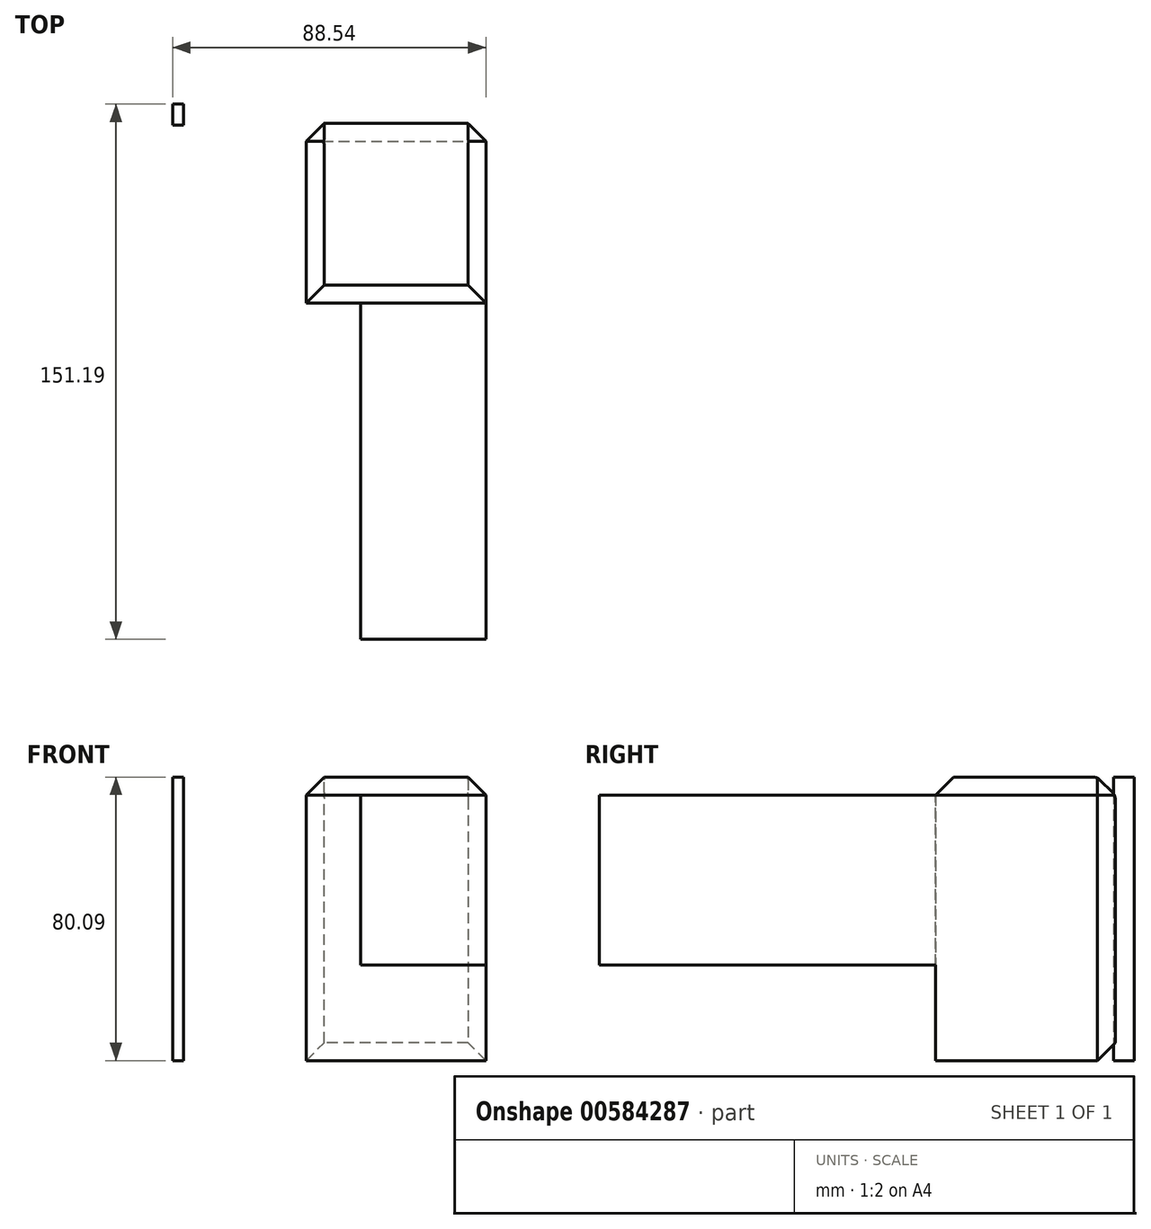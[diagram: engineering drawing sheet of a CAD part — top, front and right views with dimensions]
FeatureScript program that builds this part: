
annotation { "Feature Type Name" : "Feature", "Feature Type Description" : "" }
export const myFeature = defineFeature(function(context is Context, id is Id, definition is map)
    precondition{}
    {
        {
            var Q0;
            Q0=qCreatedBy(makeId("Top.planeOp"),FACE);
            var sketch = newSketch(context, id + "F0", { "sketchPlane" : qUnion([Q0])});
            skLineSegment(sketch, "E0.bottom", {"start": v(-37.74, 29.84) * mm, "end": v(-34.65, 29.84) * mm});
            skLineSegment(sketch, "E0.top", {"start": v(-37.74, 23.95) * mm, "end": v(-34.65, 23.95) * mm});
            skLineSegment(sketch, "E0.left", {"start": v(-37.74, 29.84) * mm, "end": v(-37.74, 23.95) * mm});
            skLineSegment(sketch, "E0.right", {"start": v(-34.65, 29.84) * mm, "end": v(-34.65, 23.95) * mm});
            skLineSegment(sketch, "E1.bottom", {"start": v(0, 24.42) * mm, "end": v(50.8, 24.42) * mm});
            skLineSegment(sketch, "E1.top", {"start": v(0, -26.38) * mm, "end": v(50.8, -26.38) * mm});
            skLineSegment(sketch, "E1.left", {"start": v(0, 24.42) * mm, "end": v(0, -26.38) * mm});
            skLineSegment(sketch, "E1.right", {"start": v(50.8, 24.42) * mm, "end": v(50.8, -26.38) * mm});
            skSolve(sketch);
        }
        {
            var Q0;
            Q0 = qSketchRegion(id + "F0", true);
            extrude(context, id + "F1", {"entities" : qUnion([Q0]), "depth" : 80.1 * mm, "offsetDistance" : 25.4 * mm});
        }
        {
            var Q0;
            Q0=makeQuery(id+"F1.opExtrude","CAP_EDGE",EDGE,{"disambiguationData":[OSD([sQuery(id+"F0.wireOp",EDGE,"E1.top")])],"isStart":false});
            var Q1;
            Q1=makeQuery(id+"F1.opExtrude","CAP_EDGE",EDGE,{"disambiguationData":[OSD([sQuery(id+"F0.wireOp",EDGE,"E1.left")])],"isStart":false});
            var Q2;
            Q2=makeQuery(id+"F1.opExtrude","CAP_EDGE",EDGE,{"disambiguationData":[OSD([sQuery(id+"F0.wireOp",EDGE,"E1.bottom")])],"isStart":false});
            var Q3;
            Q3=makeQuery(id+"F1.opExtrude","CAP_EDGE",EDGE,{"disambiguationData":[OSD([sQuery(id+"F0.wireOp",EDGE,"E1.right")])],"isStart":false});
            var Q4;
            Q4=makeQuery(id+"F1.opExtrude","SWEPT_EDGE",EDGE,{"disambiguationData":[OSD([sQuery(id+"F0.wireOp",EDGE,"E1.bottom"),sQuery(id+"F0.wireOp",EDGE,"E1.left")])]});
            var Q5;
            Q5=makeQuery(id+"F1.opExtrude","CAP_EDGE",EDGE,{"disambiguationData":[OSD([sQuery(id+"F0.wireOp",EDGE,"E1.bottom")])],"isStart":true});
            var Q6;
            Q6=makeQuery(id+"F1.opExtrude","SWEPT_EDGE",EDGE,{"disambiguationData":[OSD([sQuery(id+"F0.wireOp",EDGE,"E1.bottom"),sQuery(id+"F0.wireOp",EDGE,"E1.right")])]});
            chamfer(context, id + "F2", {"entities" : qUnion([Q0, Q1, Q2, Q3, Q4, Q5, Q6]), "width" : 5.08 * mm, "tangentPropagation" : true});
        }
        {
            var Q0;
            {var subQ0=sQuery(id+"F0.wireOp",EDGE,"E1.bottom");Q0=makeQuery(id+"F2.opChamfer","BLEND_EDGE",EDGE,{"blendedFrom":[makeQuery(id+"F1.opExtrude","CAP_EDGE",EDGE,{"disambiguationData":[OSD([subQ0])],"isStart":false}),makeQuery(id+"F1.opExtrude","CAP_FACE",FACE,{"disambiguationData":[OSD([subQ0,sQuery(id+"F0.wireOp",EDGE,"E1.top"),sQuery(id+"F0.wireOp",EDGE,"E1.left"),sQuery(id+"F0.wireOp",EDGE,"E1.right")])],"isStart":false})],"blendedInto":[makeQuery(id+"F1.opExtrude","CAP_FACE",FACE,{"disambiguationData":[OSD([subQ0,sQuery(id+"F0.wireOp",EDGE,"E1.top"),sQuery(id+"F0.wireOp",EDGE,"E1.left"),sQuery(id+"F0.wireOp",EDGE,"E1.right")])],"isStart":false})]});}
            var Q1;
            {var subQ0=sQuery(id+"F0.wireOp",EDGE,"E1.bottom");Q1=makeQuery(id+"F2.opChamfer","BLEND_EDGE",EDGE,{"blendedFrom":[makeQuery(id+"F1.opExtrude","CAP_EDGE",EDGE,{"disambiguationData":[OSD([subQ0])],"isStart":false}),makeQuery(id+"F1.opExtrude","SWEPT_FACE",FACE,{"disambiguationData":[OSD([subQ0])]})],"blendedInto":[makeQuery(id+"F1.opExtrude","SWEPT_FACE",FACE,{"disambiguationData":[OSD([subQ0])]})]});}
            fillet(context, id + "F3", {"entities" : qUnion([Q0, Q1]), "radius" : 2.54 * mm, "tangentPropagation" : true, "allowEdgeOverflow" : false});
        }
        {
            var Q0;
            Q0=makeQuery(id+"F1.opExtrude","CAP_FACE",FACE,{"disambiguationData":[OSD([sQuery(id+"F0.wireOp",EDGE,"E1.bottom"),sQuery(id+"F0.wireOp",EDGE,"E1.top"),sQuery(id+"F0.wireOp",EDGE,"E1.left"),sQuery(id+"F0.wireOp",EDGE,"E1.right")])],"isStart":false});
            var sketch = newSketch(context, id + "F4", { "sketchPlane" : qUnion([Q0])});
            skCircle(sketch, "E2", {"center": v(0, 0) * mm, "radius": 34.99 * mm});
            skSolve(sketch);
        }
        {
            var Q0;
            Q0=sQuery(id+"F4.wireOp",EDGE,"E2");
            extrude(context, id + "F5", {"bodyType" : ToolBodyType.SURFACE, "surfaceEntities" : qUnion([Q0]), "depth" : 110.23 * mm, "offsetDistance" : 25.4 * mm});
        }
        {
            var Q0;
            Q0=makeQuery(id+"F1.opExtrude","SWEPT_FACE",FACE,{"disambiguationData":[OSD([sQuery(id+"F0.wireOp",EDGE,"E1.top")])]});
            var sketch = newSketch(context, id + "F6", { "sketchPlane" : qUnion([Q0])});
            skLineSegment(sketch, "E3.bottom", {"start": v(15.41, 27.02) * mm, "end": v(50.8, 27.02) * mm});
            skLineSegment(sketch, "E3.top", {"start": v(15.41, 75) * mm, "end": v(50.8, 75) * mm});
            skLineSegment(sketch, "E3.left", {"start": v(15.41, 27.02) * mm, "end": v(15.41, 75) * mm});
            skLineSegment(sketch, "E3.right", {"start": v(50.8, 27.02) * mm, "end": v(50.8, 75) * mm});
            skSolve(sketch);
        }
        {
            var Q0;
            Q0 = qSketchRegion(id + "F6", true);
            extrude(context, id + "F7", {"entities" : qUnion([Q0]), "operationType" : NewBodyOperationType.ADD, "depth" : 94.97 * mm, "offsetDistance" : 25.4 * mm});
        }
    });
